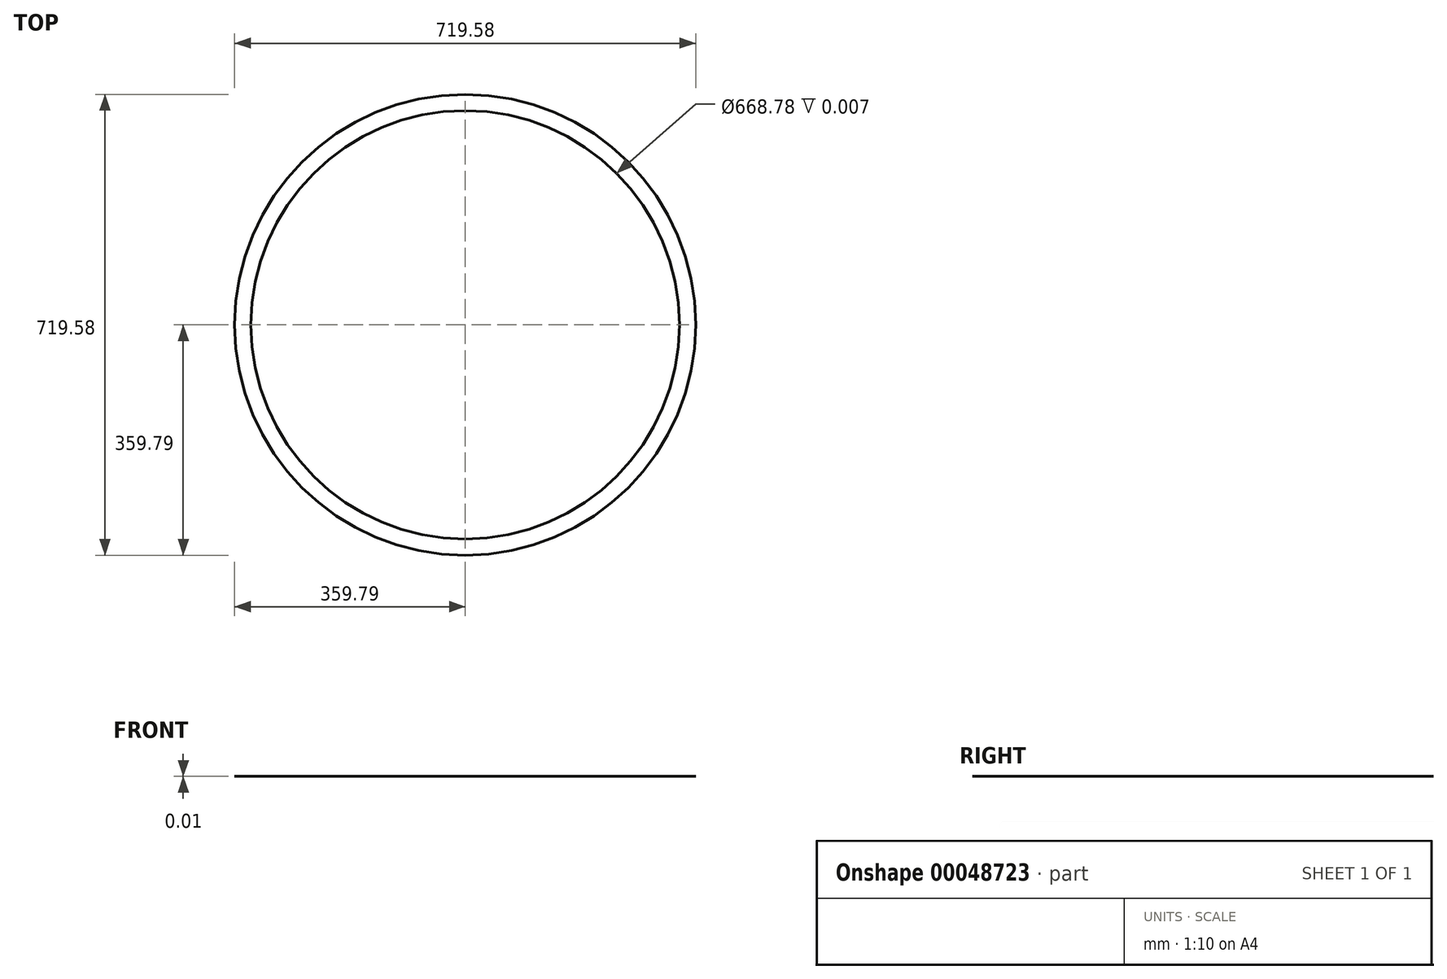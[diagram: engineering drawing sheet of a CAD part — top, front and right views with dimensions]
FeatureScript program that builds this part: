
annotation { "Feature Type Name" : "Feature", "Feature Type Description" : "" }
export const myFeature = defineFeature(function(context is Context, id is Id, definition is map)
    precondition{}
    {
        {
            var Q0;
            Q0=qCreatedBy(makeId("Top.planeOp"),FACE);
            var sketch = newSketch(context, id + "F0", { "sketchPlane" : qUnion([Q0])});
            skCircle(sketch, "E0", {"center": v(0, 0) * mm, "radius": 359.8 * mm});
            skCircle(sketch, "E1", {"center": v(0, 0) * mm, "radius": 334.4 * mm});
            skSolve(sketch);
        }
        {
            var Q0;
            Q0=makeQuery(id+"F0.imprint","IMPRINT",FACE,{"disambiguationData":[TD([[makeQuery(id+"F0.imprint","IMPRINT",EDGE,{"derivedFrom":sQuery(id+"F0.wireOp",EDGE,"E0")}),1.0]])]});
            extrude(context, id + "F1", {"entities" : qUnion([Q0]), "depth" : 3 / 406.4 * mm});
        }
    });
